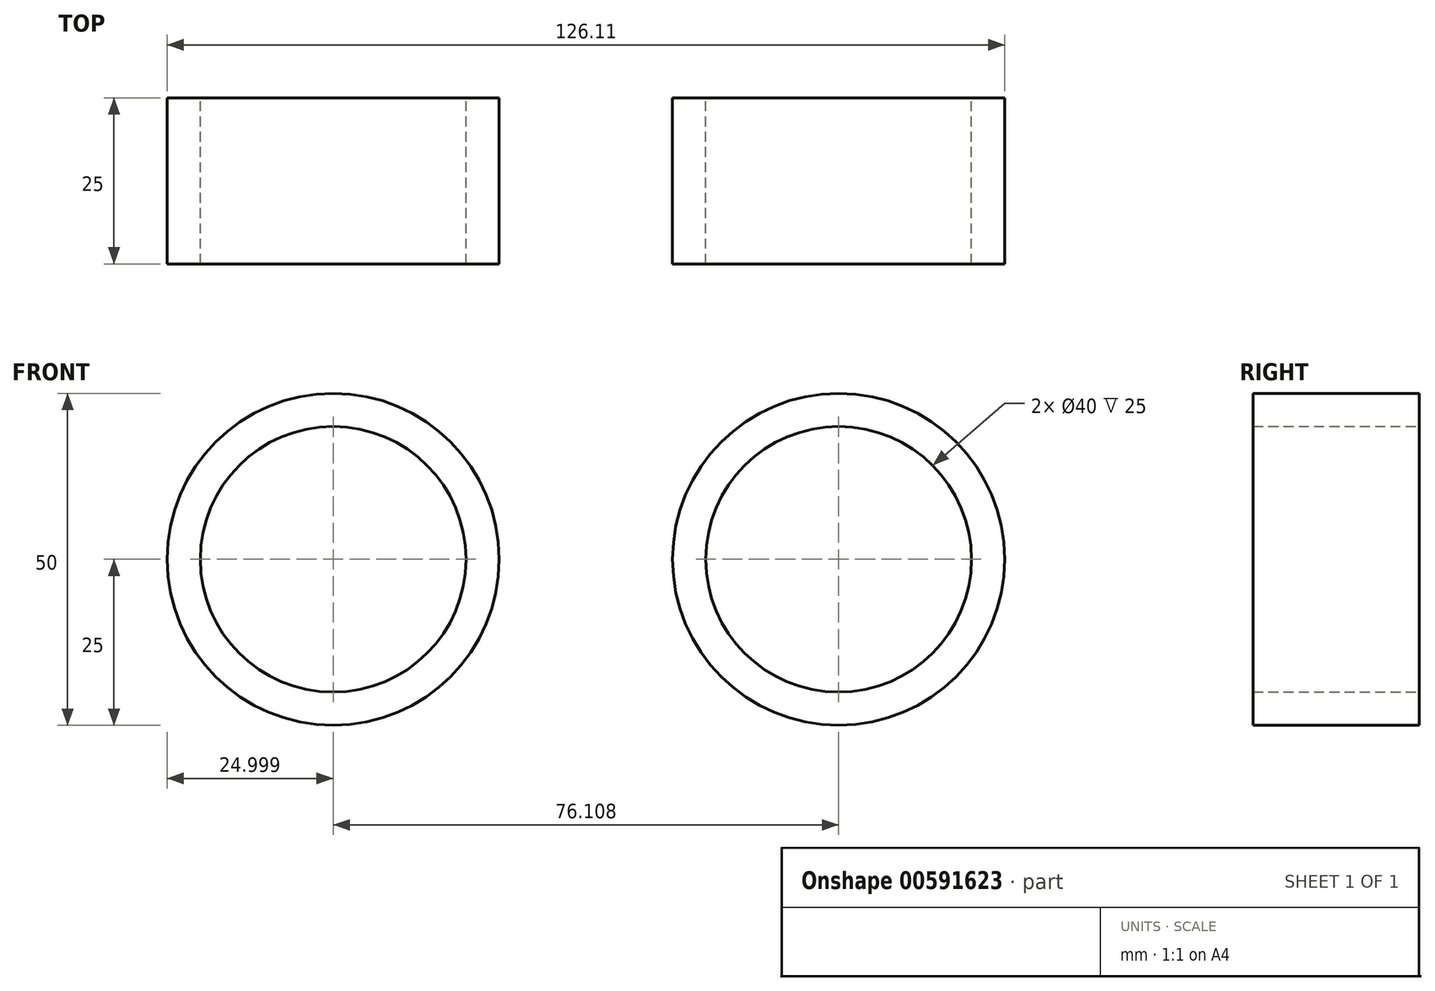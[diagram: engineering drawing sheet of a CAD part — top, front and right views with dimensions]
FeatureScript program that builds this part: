
annotation { "Feature Type Name" : "Feature", "Feature Type Description" : "" }
export const myFeature = defineFeature(function(context is Context, id is Id, definition is map)
    precondition{}
    {
        {
            var Q0;
            Q0=qCreatedBy(makeId("Front.planeOp"),FACE);
            var sketch = newSketch(context, id + "F0", { "sketchPlane" : qUnion([Q0])});
            skCircle(sketch, "E0", {"center": v(-36.91, 0) * mm, "radius": 25 * mm});
            skCircle(sketch, "E1", {"center": v(39.2, 0) * mm, "radius": 25 * mm});
            skCircle(sketch, "E2", {"center": v(-36.91, 0) * mm, "radius": 20 * mm});
            skCircle(sketch, "E3", {"center": v(39.2, 0) * mm, "radius": 20 * mm});
            skSolve(sketch);
        }
        {
            var Q0;
            Q0=makeQuery(id+"F0.imprint","IMPRINT",FACE,{"disambiguationData":[TD([[makeQuery(id+"F0.imprint","IMPRINT",EDGE,{"derivedFrom":sQuery(id+"F0.wireOp",EDGE,"E0")}),1.0]])]});
            var Q1;
            Q1=makeQuery(id+"F0.imprint","IMPRINT",FACE,{"disambiguationData":[TD([[makeQuery(id+"F0.imprint","IMPRINT",EDGE,{"derivedFrom":sQuery(id+"F0.wireOp",EDGE,"E1")}),1.0]])]});
            extrude(context, id + "F1", {"entities" : qUnion([Q0, Q1]), "depth" : 25 * mm, "offsetDistance" : 25 * mm});
        }
        {
            var Q0;
            Q0=qCreatedBy(makeId("Front.planeOp"),FACE);
            var sketch = newSketch(context, id + "F2", { "sketchPlane" : qUnion([Q0])});
            skLineSegment(sketch, "E4", {"start": v(37.97, 25.1) * mm, "end": v(-36.88, 25.1) * mm});
            skLineSegment(sketch, "E5", {"start": v(-36.88, 25.1) * mm, "end": v(-36.88, 25.1) * mm});
            skLineSegment(sketch, "E6", {"start": v(38.35, -25.19) * mm, "end": v(-37.25, -25.19) * mm});
            skLineSegment(sketch, "E7", {"start": v(21.17, 17.5) * mm, "end": v(-20.28, 17.5) * mm});
            skLineSegment(sketch, "E8", {"start": v(23.12, -19.14) * mm, "end": v(-21.52, -19.14) * mm});
            skSolve(sketch);
        }
        {
            var Q0;
            Q0=sQuery(id+"F2.wireOp",EDGE,"E4");
            var Q1;
            Q1=sQuery(id+"F2.wireOp",EDGE,"E7");
            extrude(context, id + "F3", {"bodyType" : ToolBodyType.SURFACE, "surfaceEntities" : qUnion([Q0, Q1]), "depth" : 25 * mm, "offsetDistance" : 25 * mm});
        }
    });
